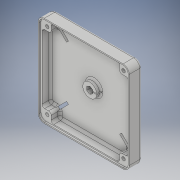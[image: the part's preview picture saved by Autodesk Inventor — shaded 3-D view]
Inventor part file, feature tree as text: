
AUTODESK INVENTOR PART (.ipt)
format: ipt  version: 2019 (Build 230136000, 136)  size: 679,424 bytes
history: native  units: mm
features: sketch x8, extrude x7, other x5, fillet x3, projected_geometry x3, reference x1
ambient origin geometry x8: Origin, YZ Plane, XZ Plane, XY Plane, X Axis, Y Axis, Z Axis, Center Point
bodies: Body1 (feature_tree)
feature tree (27):
  other  "Твердое тело1"
  extrude  "Выдавливание1"  Depth=2.5mm TaperAngle=0.0deg
  extrude  "Выдавливание2"  Depth=2.5mm
  other  "Выступ1"
  extrude  "Выдавливание3"  Depth=12.0mm TaperAngle=0.0deg
  fillet  "Сопряжение1"  Radius=6.0mm
  extrude  "Выдавливание4"  Depth=10.5mm
  fillet  "Сопряжение3"  Radius=6.0mm
  extrude  "Выдавливание5"  Depth=10.5mm
  sketch  "Эскиз6"
  extrude  "Выдавливание6"  Depth=6.0mm
  fillet  "Сопряжение4"  Radius=10.5mm
  extrude  "Выдавливание7"  Depth=10.0mm TaperAngle=0.0deg
  sketch  "Эскиз1"
  sketch  "Эскиз2"
  projected_geometry  "Спроецированная петля1"
  sketch  "Эскиз3"
  projected_geometry  "Спроецированная петля2"
  sketch  "Эскиз4"
  sketch  "Эскиз5"
  reference  "Ссылка1"
  sketch  "Эскиз7"
  sketch  "Эскиз8"
  projected_geometry  "Спроецированная петля3"
  other  "<userpath>\Documents\GitHub\Tesla_coil_V1\3dModels\TeslaCoil.iam"
  other  "TeslaCoil.iam"
  other  "RackeSecondary:1"
